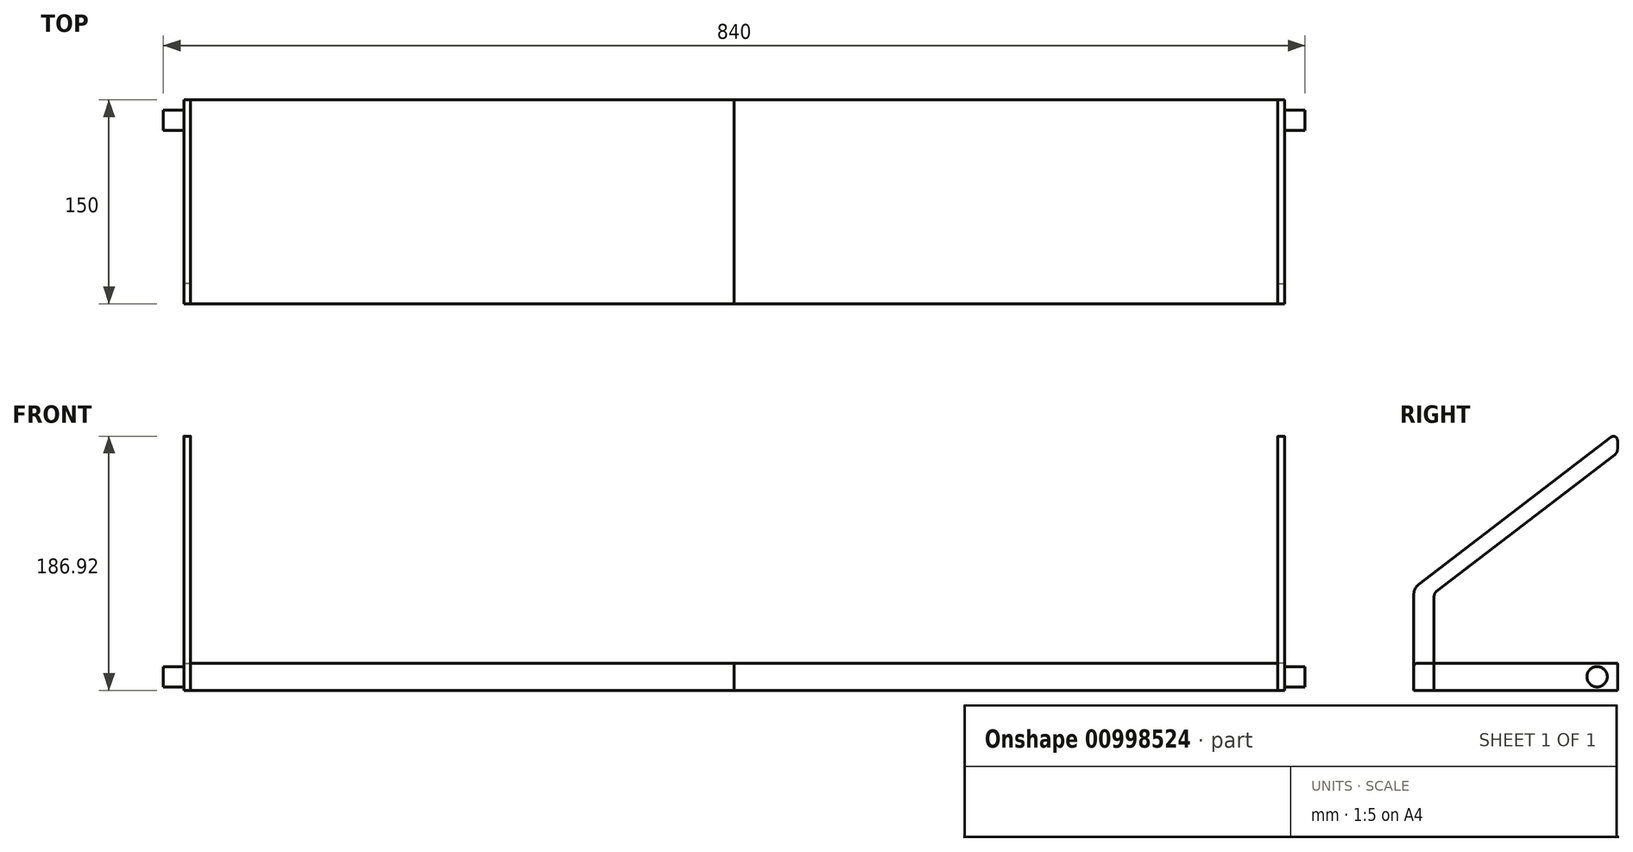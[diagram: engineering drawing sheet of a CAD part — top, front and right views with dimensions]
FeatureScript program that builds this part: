
annotation { "Feature Type Name" : "Feature", "Feature Type Description" : "" }
export const myFeature = defineFeature(function(context is Context, id is Id, definition is map)
    precondition{}
    {
        {
            var Q0;
            Q0=qCreatedBy(makeId("Right.planeOp"),FACE);
            var sketch = newSketch(context, id + "F0", { "sketchPlane" : qUnion([Q0])});
            skLineSegment(sketch, "E0.bottom", {"start": v(0, 0) * mm, "end": v(-150, 0) * mm});
            skLineSegment(sketch, "E0.top", {"start": v(0, 20) * mm, "end": v(-150, 20) * mm});
            skLineSegment(sketch, "E0.left", {"start": v(0, 0) * mm, "end": v(0, 20) * mm});
            skLineSegment(sketch, "E0.right", {"start": v(-150, 0) * mm, "end": v(-150, 20) * mm});
            skPoint(sketch, "E0.middle", {"position": v(-75, 10) * mm});
            skLineSegment(sketch, "E1", {"start": v(-150, 0) * mm, "end": v(-150, 70.07) * mm});
            skLineSegment(sketch, "E2", {"start": v(-146.08, 78) * mm, "end": v(-4.83, 186.3) * mm});
            skLineSegment(sketch, "E3", {"start": v(0, 183.92) * mm, "end": v(0, 177.35) * mm});
            skLineSegment(sketch, "E4", {"start": v(-1.96, 173.38) * mm, "end": v(-133.04, 72.88) * mm});
            skLineSegment(sketch, "E5", {"start": v(-135, 68.91) * mm, "end": v(-135, 0) * mm});
            skLineSegment(sketch, "E6", {"start": v(-135, 0) * mm, "end": v(-150, 0) * mm});
            skPoint(sketch, "E7.visualSharp", {"position": v(-150, 75) * mm});
            skArc(sketch, "E7.filletArc", {"start": v(-146.08, 78) * mm, "mid": v(-148.97, 74.5) * mm, "end": v(-150, 70.07) * mm});
            skPoint(sketch, "E8.visualSharp", {"position": v(-135, 71.38) * mm});
            skArc(sketch, "E8.filletArc", {"start": v(-133.04, 72.88) * mm, "mid": v(-134.48, 71.12) * mm, "end": v(-135, 68.91) * mm});
            skPoint(sketch, "E9.visualSharp", {"position": v(0, 174.88) * mm});
            skArc(sketch, "E9.filletArc", {"start": v(-1.96, 173.38) * mm, "mid": v(-0.52, 175.13) * mm, "end": v(0, 177.35) * mm});
            skPoint(sketch, "E10.visualSharp", {"position": v(0, 190) * mm});
            skArc(sketch, "E10.filletArc", {"start": v(0, 183.92) * mm, "mid": v(-1.67, 186.61) * mm, "end": v(-4.83, 186.3) * mm});
            skSolve(sketch);
        }
        {
            var Q0;
            {var subQ0=sQuery(id+"F0.wireOp",EDGE,"E0.bottom");Q0=makeQuery(id+"F0.imprint","IMPRINT",FACE,{"disambiguationData":[TD([[makeQuery(id+"F0.imprint","IMPRINT",EDGE,{"derivedFrom":subQ0}),-1.0]])]});}
            var Q1;
            {var subQ5=sQuery(id+"F0.wireOp",EDGE,"E6");Q1=makeQuery(id+"F0.imprint","IMPRINT",FACE,{"disambiguationData":[TD([[makeQuery(id+"F0.imprint","IMPRINT",EDGE,{"derivedFrom":subQ5}),-1.0]])]});}
            extrude(context, id + "F1", {"entities" : qUnion([Q0, Q1]), "depth" : 405 * mm, "offsetDistance" : 25 * mm});
        }
        {
            var Q0;
            Q0=makeQuery(id+"F1.opExtrude","CAP_FACE",FACE,{"disambiguationData":[OSD([sQuery(id+"F0.wireOp",EDGE,"E0.bottom"),sQuery(id+"F0.wireOp",EDGE,"E0.top"),sQuery(id+"F0.wireOp",EDGE,"E0.left"),sQuery(id+"F0.wireOp",EDGE,"E1"),sQuery(id+"F0.wireOp",EDGE,"E6")])],"isStart":false});
            var sketch = newSketch(context, id + "F2", { "sketchPlane" : qUnion([Q0])});
            skLineSegment(sketch, "E11.0.0", {"start": v(-4.83, 186.3) * mm, "end": v(-146.08, 78) * mm});
            skArc(sketch, "E11.0.1", {"start": v(-146.08, 78) * mm, "mid": v(-148.97, 74.5) * mm, "end": v(-150, 70.07) * mm});
            skLineSegment(sketch, "E11.0.2", {"start": v(-150, 70.07) * mm, "end": v(-150, 20) * mm});
            skLineSegment(sketch, "E11.0.3", {"start": v(-150, 20) * mm, "end": v(-135, 20) * mm});
            skLineSegment(sketch, "E11.0.4", {"start": v(-135, 20) * mm, "end": v(-135, 68.91) * mm});
            skArc(sketch, "E11.0.5", {"start": v(-135, 68.91) * mm, "mid": v(-134.48, 71.12) * mm, "end": v(-133.04, 72.88) * mm});
            skLineSegment(sketch, "E11.0.6", {"start": v(-133.04, 72.88) * mm, "end": v(-1.96, 173.38) * mm});
            skArc(sketch, "E11.0.7", {"start": v(-1.96, 173.38) * mm, "mid": v(-0.52, 175.13) * mm, "end": v(0, 177.35) * mm});
            skLineSegment(sketch, "E11.0.8", {"start": v(0, 177.35) * mm, "end": v(0, 183.92) * mm});
            skArc(sketch, "E11.0.9", {"start": v(0, 183.92) * mm, "mid": v(-1.67, 186.61) * mm, "end": v(-4.83, 186.3) * mm});
            skLineSegment(sketch, "E11.1.0", {"start": v(-150, 0) * mm, "end": v(-135, 0) * mm});
            skLineSegment(sketch, "E11.1.1", {"start": v(-135, 0) * mm, "end": v(-135, 20) * mm});
            skLineSegment(sketch, "E11.1.2", {"start": v(-135, 20) * mm, "end": v(-150, 20) * mm});
            skLineSegment(sketch, "E11.1.3", {"start": v(-150, 20) * mm, "end": v(-150, 0) * mm});
            skSolve(sketch);
        }
        {
            var Q0;
            Q0=qSketchRegion(id+"F2",true);
            extrude(context, id + "F3", {"entities" : qUnion([Q0]), "oppositeDirection" : true, "depth" : 5 * mm, "offsetDistance" : 25 * mm});
        }
        {
            var Q0;
            Q0=makeQuery(id+"F1.opExtrude","SWEPT_EDGE",EDGE,{"disambiguationData":[OSD([sQuery(id+"F0.wireOp",EDGE,"E0.top"),sQuery(id+"F0.wireOp",EDGE,"E1")])]});
            var Q1;
            Q1=makeQuery(id+"F1.opExtrude","SWEPT_EDGE",EDGE,{"disambiguationData":[OSD([sQuery(id+"F0.wireOp",EDGE,"E1"),sQuery(id+"F0.wireOp",EDGE,"E6")])]});
            fillet(context, id + "F4", {"entities" : qUnion([Q0, Q1]), "radius" : 3 * mm, "tangentPropagation" : true, "allowEdgeOverflow" : false});
        }
        {
            var Q0;
            Q0=makeQuery(id+"F1.opExtrude","CAP_FACE",FACE,{"disambiguationData":[OSD([sQuery(id+"F0.wireOp",EDGE,"E0.bottom"),sQuery(id+"F0.wireOp",EDGE,"E0.top"),sQuery(id+"F0.wireOp",EDGE,"E0.left"),sQuery(id+"F0.wireOp",EDGE,"E1"),sQuery(id+"F0.wireOp",EDGE,"E6")])],"isStart":false});
            var sketch = newSketch(context, id + "F5", { "sketchPlane" : qUnion([Q0])});
            skLineSegment(sketch, "E12", {"start": v(-30, 20) * mm, "end": v(-30, 0) * mm, "construction": true});
            skLineSegment(sketch, "E13", {"start": v(-30, 10) * mm, "end": v(0, 10) * mm, "construction": true});
            skCircle(sketch, "E14", {"center": v(-15, 10) * mm, "radius": 7.5 * mm});
            skSolve(sketch);
        }
        {
            var Q0;
            Q0=qSketchRegion(id+"F5",true);
            extrude(context, id + "F6", {"entities" : qUnion([Q0]), "operationType" : NewBodyOperationType.ADD, "depth" : 15 * mm, "offsetDistance" : 25 * mm});
        }
        {
            var Q0;
            Q0=makeQuery(id+"F1.opExtrude","SWEPT_BODY",BODY,{"disambiguationData":[OSD([sQuery(id+"F0.wireOp",EDGE,"E0.bottom"),sQuery(id+"F0.wireOp",EDGE,"E0.top"),sQuery(id+"F0.wireOp",EDGE,"E0.left"),sQuery(id+"F0.wireOp",EDGE,"E1"),sQuery(id+"F0.wireOp",EDGE,"E6")])]});
            var Q1;
            Q1=makeQuery(id+"F3.opExtrude","SWEPT_BODY",BODY,{"disambiguationData":[OSD([sQuery(id+"F2.wireOp",EDGE,"E11.0.0"),sQuery(id+"F2.wireOp",EDGE,"E11.0.1"),sQuery(id+"F2.wireOp",EDGE,"E11.0.2"),sQuery(id+"F2.wireOp",EDGE,"E11.0.4"),sQuery(id+"F2.wireOp",EDGE,"E11.0.5"),sQuery(id+"F2.wireOp",EDGE,"E11.0.6"),sQuery(id+"F2.wireOp",EDGE,"E11.0.7"),sQuery(id+"F2.wireOp",EDGE,"E11.0.8"),sQuery(id+"F2.wireOp",EDGE,"E11.0.9"),sQuery(id+"F2.wireOp",EDGE,"E11.1.0"),sQuery(id+"F2.wireOp",EDGE,"E11.1.1"),sQuery(id+"F2.wireOp",EDGE,"E11.1.3")])]});
            var Q2;
            Q2=qCreatedBy(makeId("Right.planeOp"),FACE);
            mirror(context, id + "F7", {"entities" : qUnion([Q0, Q1]), "mirrorPlane" : qUnion([Q2])});
        }
    });
